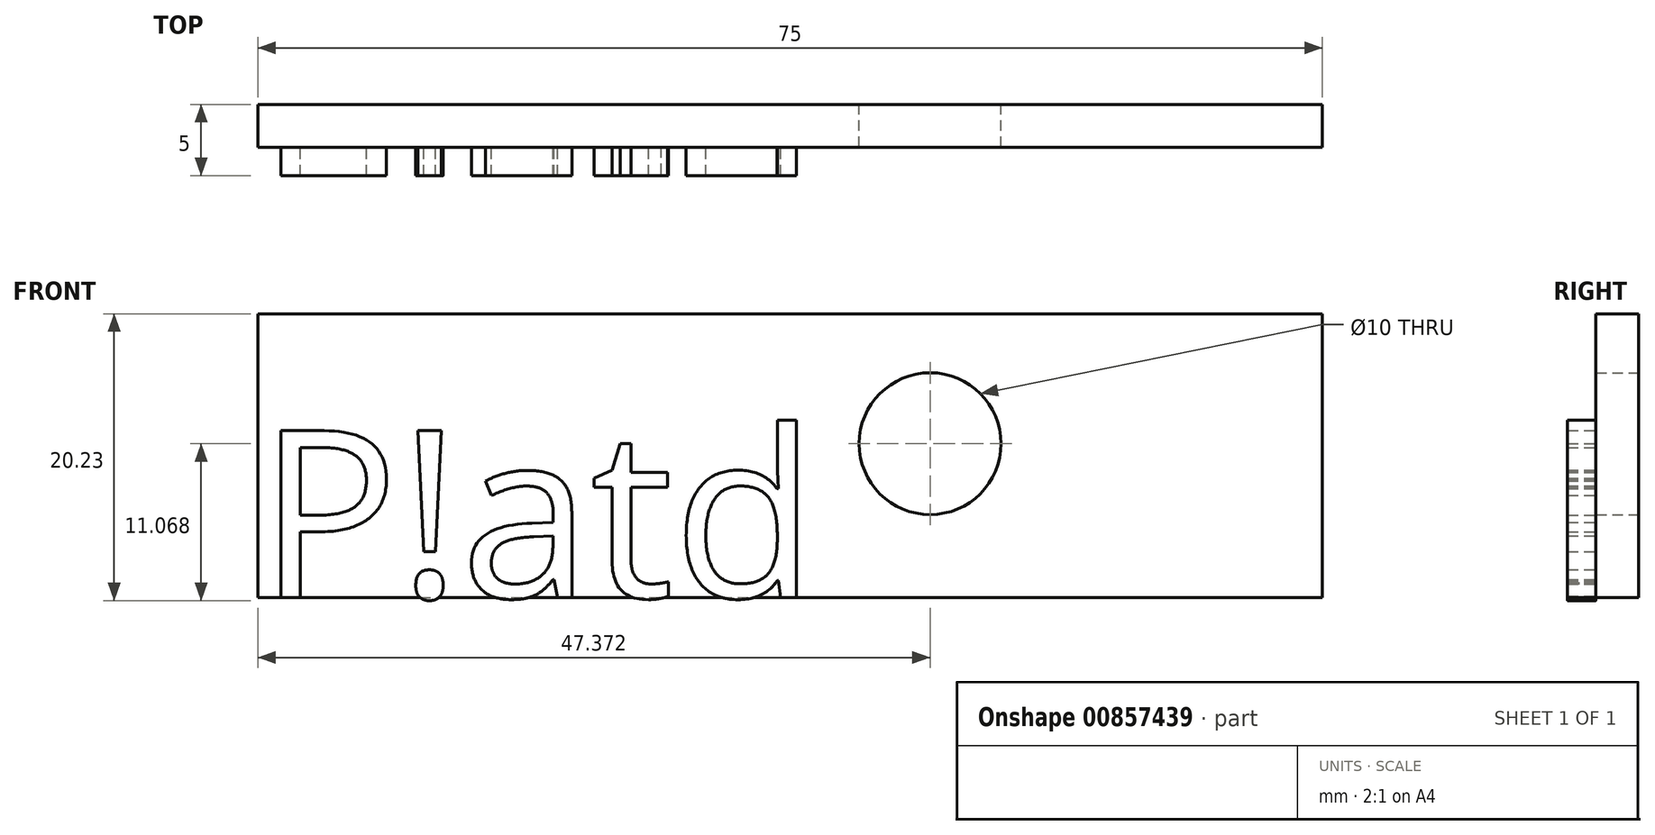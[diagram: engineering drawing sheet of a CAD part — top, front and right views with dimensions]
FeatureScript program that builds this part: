
annotation { "Feature Type Name" : "Feature", "Feature Type Description" : "" }
export const myFeature = defineFeature(function(context is Context, id is Id, definition is map)
    precondition{}
    {
        {
            var Q0;
            Q0=qCreatedBy(makeId("Front.planeOp"),FACE);
            var sketch = newSketch(context, id + "F0", { "sketchPlane" : qUnion([Q0])});
            skLineSegment(sketch, "E0.bottom", {"start": v(0, 20) * mm, "end": v(75, 20) * mm});
            skLineSegment(sketch, "E0.top", {"start": v(0, 0) * mm, "end": v(75, 0) * mm});
            skLineSegment(sketch, "E0.left", {"start": v(0, 20) * mm, "end": v(0, 0) * mm});
            skLineSegment(sketch, "E0.right", {"start": v(75, 20) * mm, "end": v(75, 0) * mm});
            skCircle(sketch, "E1", {"center": v(47.37, 10.84) * mm, "radius": 5 * mm});
            skSolve(sketch);
        }
        {
            var Q0;
            Q0 = qSketchRegion(id + "F0", true);
            extrude(context, id + "F1", {"entities" : qUnion([Q0]), "depth" : 3 * mm, "offsetDistance" : 25 * mm});
        }
        {
            var Q0;
            Q0=makeQuery(id+"F1.opExtrude","CAP_FACE",FACE,{"disambiguationData":[OSD([sQuery(id+"F0.wireOp",EDGE,"E0.bottom"),sQuery(id+"F0.wireOp",EDGE,"E0.top"),sQuery(id+"F0.wireOp",EDGE,"E0.left"),sQuery(id+"F0.wireOp",EDGE,"E0.right"),sQuery(id+"F0.wireOp",EDGE,"E1")])],"isStart":false});
            var sketch = newSketch(context, id + "F2", { "sketchPlane" : qUnion([Q0])});
            skSolve(sketch);
        }
        {
            var Q0;
            Q0=makeQuery(id+"F2.imprint","IMPRINT",FACE,{"disambiguationData":[TD([[makeQuery(id+"F2.imprint","IMPRINT",EDGE,{"derivedFrom":makeQuery(id+"F1.opExtrude","CAP_EDGE",EDGE,{"disambiguationData":[OSD([sQuery(id+"F0.wireOp",EDGE,"E0.bottom")])],"isStart":false})}),-1.0]])]});
            var sketch = newSketch(context, id + "F3", { "sketchPlane" : qUnion([Q0])});
            skSolve(sketch);
        }
        {
            var Q0;
            Q0=makeQuery(id+"F3.imprint","IMPRINT",FACE,{"disambiguationData":[TD([[makeQuery(id+"F3.imprint","IMPRINT",EDGE,{"derivedFrom":makeQuery(id+"F2.imprint","IMPRINT",EDGE,{"derivedFrom":makeQuery(id+"F1.opExtrude","CAP_EDGE",EDGE,{"disambiguationData":[OSD([sQuery(id+"F0.wireOp",EDGE,"E0.bottom")])],"isStart":false})})}),-1.0]])]});
            var sketch = newSketch(context, id + "F4", { "sketchPlane" : qUnion([Q0])});
            skSolve(sketch);
        }
        {
            var Q0;
            Q0=makeQuery(id+"F4.imprint","IMPRINT",FACE,{"disambiguationData":[TD([[makeQuery(id+"F4.imprint","IMPRINT",EDGE,{"derivedFrom":makeQuery(id+"F3.imprint","IMPRINT",EDGE,{"derivedFrom":makeQuery(id+"F2.imprint","IMPRINT",EDGE,{"derivedFrom":makeQuery(id+"F1.opExtrude","CAP_EDGE",EDGE,{"disambiguationData":[OSD([sQuery(id+"F0.wireOp",EDGE,"E0.bottom")])],"isStart":false})})})}),-1.0]])]});
            var sketch = newSketch(context, id + "F5", { "sketchPlane" : qUnion([Q0])});
            skText(sketch, "E2", { "text": "P!atd", "fontName": "OpenSans-Regular.ttf"});
            const initialGuessF5  = {"E2": [0, 0, 1, 0, 0.01185]};
            skSetInitialGuess(sketch, initialGuessF5);
            skSolve(sketch);
        }
        {
            var Q0;
            Q0 = qSketchRegion(id + "F5", true);
            extrude(context, id + "F6", {"entities" : qUnion([Q0]), "operationType" : NewBodyOperationType.ADD, "depth" : 2 * mm, "offsetDistance" : 25 * mm});
        }
    });
